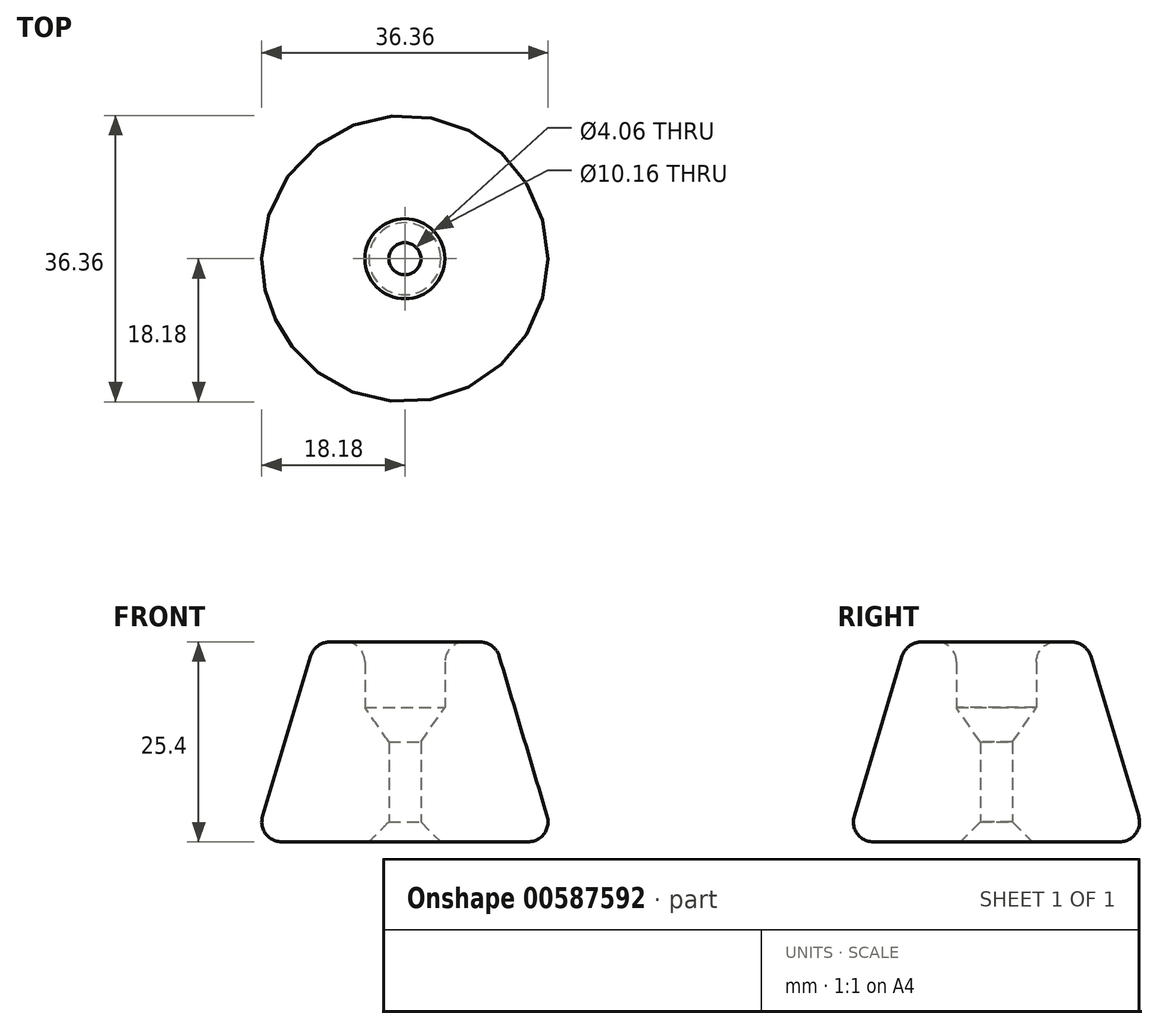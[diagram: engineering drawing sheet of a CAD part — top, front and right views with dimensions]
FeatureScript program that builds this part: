
annotation { "Feature Type Name" : "Feature", "Feature Type Description" : "" }
export const myFeature = defineFeature(function(context is Context, id is Id, definition is map)
    precondition{}
    {
        {
            var Q0;
            Q0=qCreatedBy(makeId("Front.planeOp"),FACE);
            var sketch = newSketch(context, id + "F0", { "sketchPlane" : qUnion([Q0])});
            skLineSegment(sketch, "E0", {"start": v(2.03, 0) * mm, "end": v(19.05, 0) * mm});
            skLineSegment(sketch, "E1", {"start": v(19.05, 0) * mm, "end": v(11.43, 25.4) * mm});
            skLineSegment(sketch, "E2", {"start": v(11.43, 25.4) * mm, "end": v(5.08, 25.4) * mm});
            skLineSegment(sketch, "E3", {"start": v(2.03, 0) * mm, "end": v(2.03, 12.7) * mm});
            skLineSegment(sketch, "E4", {"start": v(2.03, 12.7) * mm, "end": v(5.08, 17.05) * mm});
            skLineSegment(sketch, "E5", {"start": v(5.08, 17.05) * mm, "end": v(5.08, 25.4) * mm});
            skLineSegment(sketch, "E6", {"start": v(3.81, 15.24) * mm, "end": v(3.81, 17.28) * mm, "construction": true});
            skSolve(sketch);
        }
        {
            var Q0;
            Q0=qCreatedBy(makeId("Front.planeOp"),FACE);
            var sketch = newSketch(context, id + "F1", { "sketchPlane" : qUnion([Q0])});
            skLineSegment(sketch, "E7", {"start": v(0, 0) * mm, "end": v(0, 33.36) * mm});
            skSolve(sketch);
        }
        {
            var Q0;
            Q0 = qSketchRegion(id + "F0", true);
            var Q1;
            Q1=sQuery(id+"F1.wireOp",EDGE,"E7");
            revolve(context, id + "F2", {"entities" : qUnion([Q0]), "axis" : qUnion([Q1]), "revolveType" : RevolveType.FULL});
        }
        {
            var Q0;
            Q0=makeQuery(id+"F2.opRevolve","SWEPT_EDGE",EDGE,{"disambiguationData":[OSD([sQuery(id+"F0.wireOp",EDGE,"E1"),sQuery(id+"F0.wireOp",EDGE,"E2")])]});
            var Q1;
            Q1=makeQuery(id+"F2.opRevolve","SWEPT_EDGE",EDGE,{"disambiguationData":[OSD([sQuery(id+"F0.wireOp",EDGE,"E2"),sQuery(id+"F0.wireOp",EDGE,"E5")])]});
            var Q2;
            Q2=makeQuery(id+"F2.opRevolve","SWEPT_EDGE",EDGE,{"disambiguationData":[OSD([sQuery(id+"F0.wireOp",EDGE,"E0"),sQuery(id+"F0.wireOp",EDGE,"E1")])]});
            fillet(context, id + "F3", {"entities" : qUnion([Q0, Q1, Q2]), "radius" : 2.54 * mm, "tangentPropagation" : true, "allowEdgeOverflow" : false});
        }
        {
            var Q0;
            Q0=makeQuery(id+"F2.opRevolve","SWEPT_EDGE",EDGE,{"disambiguationData":[OSD([sQuery(id+"F0.wireOp",EDGE,"E0"),sQuery(id+"F0.wireOp",EDGE,"E3")])]});
            chamfer(context, id + "F4", {"entities" : qUnion([Q0]), "width" : 2.54 * mm, "tangentPropagation" : true});
        }
    });
